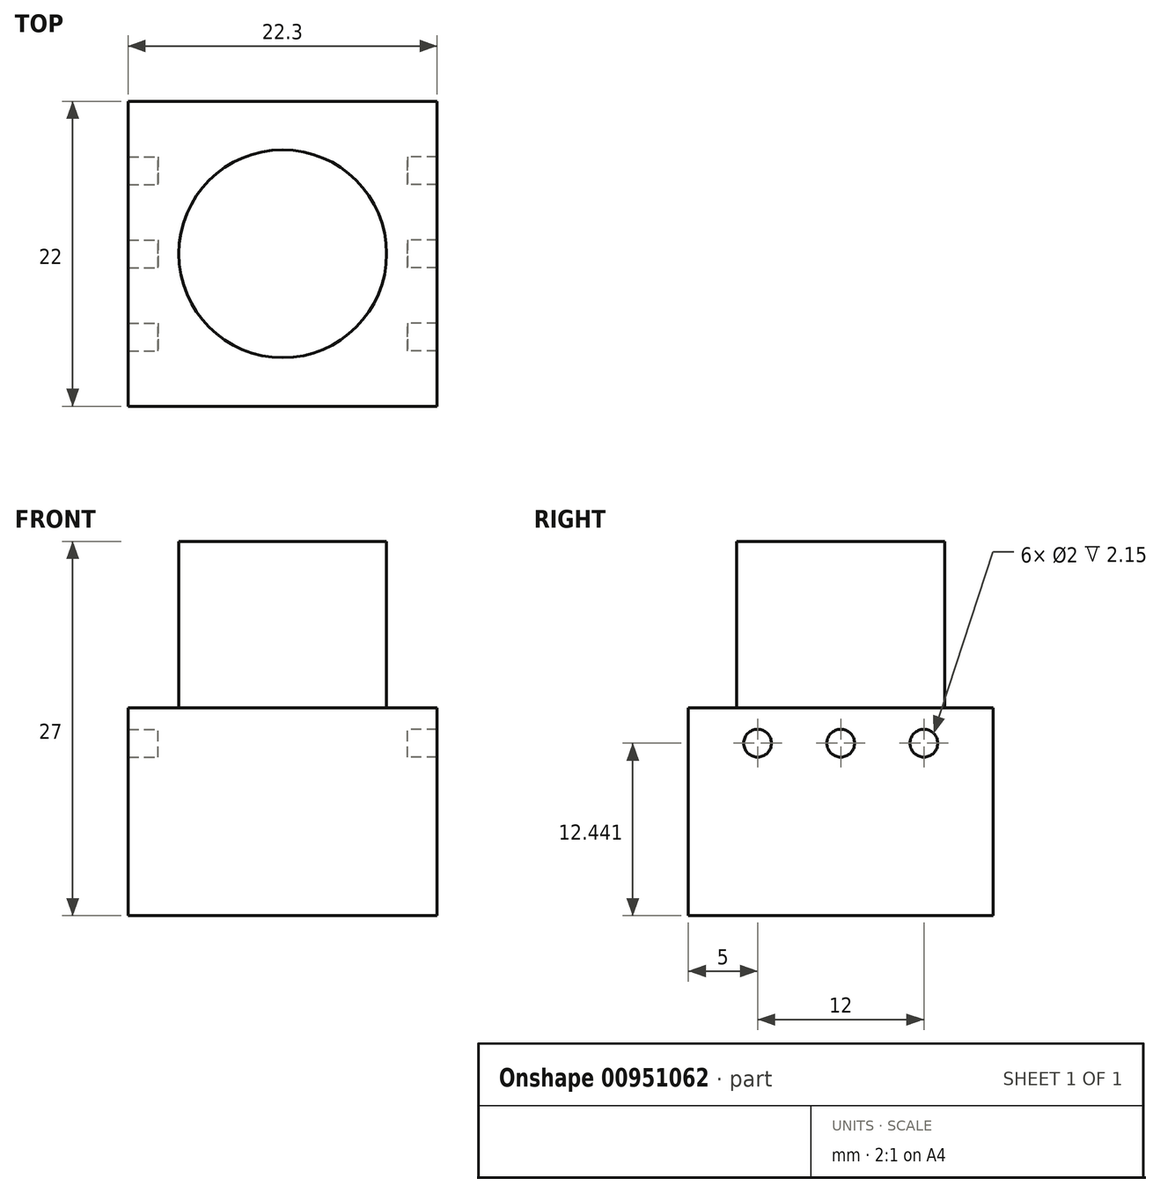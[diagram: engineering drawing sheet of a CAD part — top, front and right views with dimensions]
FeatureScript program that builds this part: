
annotation { "Feature Type Name" : "Feature", "Feature Type Description" : "" }
export const myFeature = defineFeature(function(context is Context, id is Id, definition is map)
    precondition{}
    {
        {
            var Q0;
            Q0=qCreatedBy(makeId("Top.planeOp"),FACE);
            var sketch = newSketch(context, id + "F0", { "sketchPlane" : qUnion([Q0])});
            skLineSegment(sketch, "E0.bottom", {"start": v(11.15, 11) * mm, "end": v(-11.15, 11) * mm});
            skLineSegment(sketch, "E0.top", {"start": v(11.15, -11) * mm, "end": v(-11.15, -11) * mm});
            skLineSegment(sketch, "E0.left", {"start": v(11.15, 11) * mm, "end": v(11.15, -11) * mm});
            skLineSegment(sketch, "E0.right", {"start": v(-11.15, 11) * mm, "end": v(-11.15, -11) * mm});
            skPoint(sketch, "E0.middle", {"position": v(0, 0) * mm});
            skSolve(sketch);
        }
        {
            var Q0;
            Q0=qSketchRegion(id+"F0",true);
            extrude(context, id + "F1", {"entities" : qUnion([Q0]), "depth" : 15 * mm, "offsetDistance" : 25 * mm});
        }
        {
            var Q0;
            Q0=qCreatedBy(makeId("Top.planeOp"),FACE);
            var sketch = newSketch(context, id + "F2", { "sketchPlane" : qUnion([Q0])});
            skCircle(sketch, "E1", {"center": v(0, 0) * mm, "radius": 7.5 * mm});
            skSolve(sketch);
        }
        {
            var Q0;
            Q0=qSketchRegion(id+"F2",true);
            extrude(context, id + "F3", {"entities" : qUnion([Q0]), "operationType" : NewBodyOperationType.ADD, "depth" : 27 * mm, "offsetDistance" : 25 * mm, "hasSecondDirection" : true, "secondDirectionOppositeDirection" : false, "secondDirectionDepth" : 15 * mm});
        }
        {
            var Q0;
            Q0=qCreatedBy(makeId("Right.planeOp"),FACE);
            var sketch = newSketch(context, id + "F4", { "sketchPlane" : qUnion([Q0])});
            skLineSegment(sketch, "E2", {"start": v(0, 12.44) * mm, "end": v(6, 12.44) * mm, "construction": true});
            skLineSegment(sketch, "E3", {"start": v(0, 12.44) * mm, "end": v(-6, 12.44) * mm, "construction": true});
            skCircle(sketch, "E4", {"center": v(6, 12.44) * mm, "radius": 1 * mm});
            skCircle(sketch, "E5", {"center": v(0, 12.44) * mm, "radius": 1 * mm});
            skCircle(sketch, "E6", {"center": v(-6, 12.44) * mm, "radius": 1 * mm});
            skSolve(sketch);
        }
        {
            var Q0;
            Q0=qSketchRegion(id+"F4",true);
            extrude(context, id + "F5", {"entities" : qUnion([Q0]), "operationType" : NewBodyOperationType.REMOVE, "oppositeDirection" : true, "depth" : 12 * mm, "offsetDistance" : 25 * mm, "hasSecondDirection" : true, "secondDirectionOppositeDirection" : true, "secondDirectionDepth" : 9 * mm});
        }
        {
            var Q0;
            Q0=qSketchRegion(id+"F4",true);
            extrude(context, id + "F6", {"entities" : qUnion([Q0]), "operationType" : NewBodyOperationType.REMOVE, "depth" : 13 * mm, "offsetDistance" : 25 * mm, "hasSecondDirection" : true, "secondDirectionOppositeDirection" : false, "secondDirectionDepth" : 9 * mm});
        }
    });
